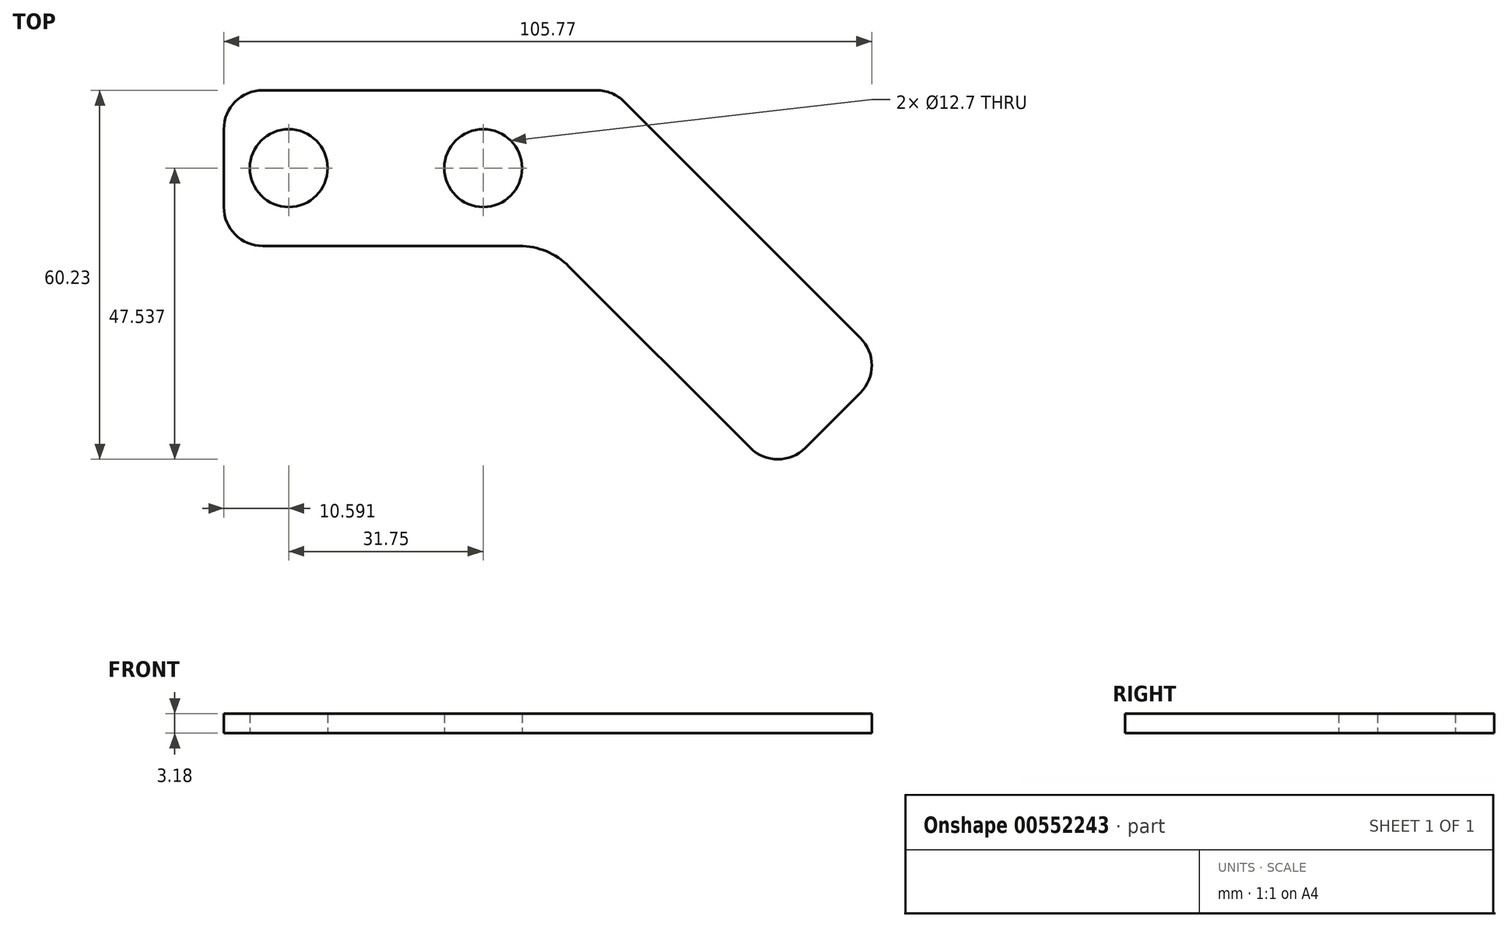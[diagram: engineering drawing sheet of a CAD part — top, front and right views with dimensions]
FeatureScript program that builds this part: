
annotation { "Feature Type Name" : "Feature", "Feature Type Description" : "" }
export const myFeature = defineFeature(function(context is Context, id is Id, definition is map)
    precondition{}
    {
        {
            var Q0;
            Q0=qCreatedBy(makeId("Top.planeOp"),FACE);
            var sketch = newSketch(context, id + "F0", { "sketchPlane" : qUnion([Q0])});
            skPoint(sketch, "E0.middle", {"position": v(6.11, 11.72) * mm});
            skLineSegment(sketch, "E1", {"start": v(59.23, -24.98) * mm, "end": v(50.25, -33.96) * mm});
            skLineSegment(sketch, "E2", {"start": v(-44.68, 5.36) * mm, "end": v(-44.68, 11.72) * mm});
            skCircle(sketch, "E3", {"center": v(-34.09, 11.72) * mm, "radius": 6.35 * mm});
            skCircle(sketch, "E4", {"center": v(-2.34, 11.72) * mm, "radius": 6.35 * mm});
            skLineSegment(sketch, "E5", {"start": v(20.68, 22.55) * mm, "end": v(59.23, -16) * mm});
            skLineSegment(sketch, "E6", {"start": v(-38.33, 24.41) * mm, "end": v(16.19, 24.41) * mm});
            skLineSegment(sketch, "E7", {"start": v(-38.33, -0.99) * mm, "end": v(3.56, -0.99) * mm});
            skLineSegment(sketch, "E8", {"start": v(11.64, -4.33) * mm, "end": v(41.27, -33.96) * mm});
            skArc(sketch, "E9.filletArc", {"start": v(-44.68, 5.36) * mm, "mid": v(-42.82, 0.87) * mm, "end": v(-38.33, -0.99) * mm});
            skArc(sketch, "E10.filletArc", {"start": v(-38.33, 24.41) * mm, "mid": v(-42.82, 22.55) * mm, "end": v(-44.68, 18.06) * mm});
            skArc(sketch, "E11.filletArc", {"start": v(20.68, 22.55) * mm, "mid": v(18.62, 23.93) * mm, "end": v(16.19, 24.41) * mm});
            skArc(sketch, "E12.filletArc", {"start": v(59.23, -24.98) * mm, "mid": v(61.09, -20.49) * mm, "end": v(59.23, -16) * mm});
            skArc(sketch, "E13.filletArc", {"start": v(41.27, -33.96) * mm, "mid": v(45.76, -35.82) * mm, "end": v(50.25, -33.96) * mm});
            skArc(sketch, "E14.filletArc", {"start": v(11.64, -4.33) * mm, "mid": v(7.93, -1.86) * mm, "end": v(3.56, -0.99) * mm});
            skLineSegment(sketch, "E15", {"start": v(-44.68, 11.72) * mm, "end": v(-44.68, 18.06) * mm});
            skSolve(sketch);
        }
        {
            var Q0;
            Q0=makeQuery(id+"F0.imprint","IMPRINT",FACE,{"disambiguationData":[TD([[makeQuery(id+"F0.imprint","IMPRINT",EDGE,{"derivedFrom":sQuery(id+"F0.wireOp",EDGE,"E1")}),-1.0]])]});
            extrude(context, id + "F1", {"entities" : qUnion([Q0]), "depth" : 3.17 * mm, "offsetDistance" : 25.4 * mm});
        }
    });
